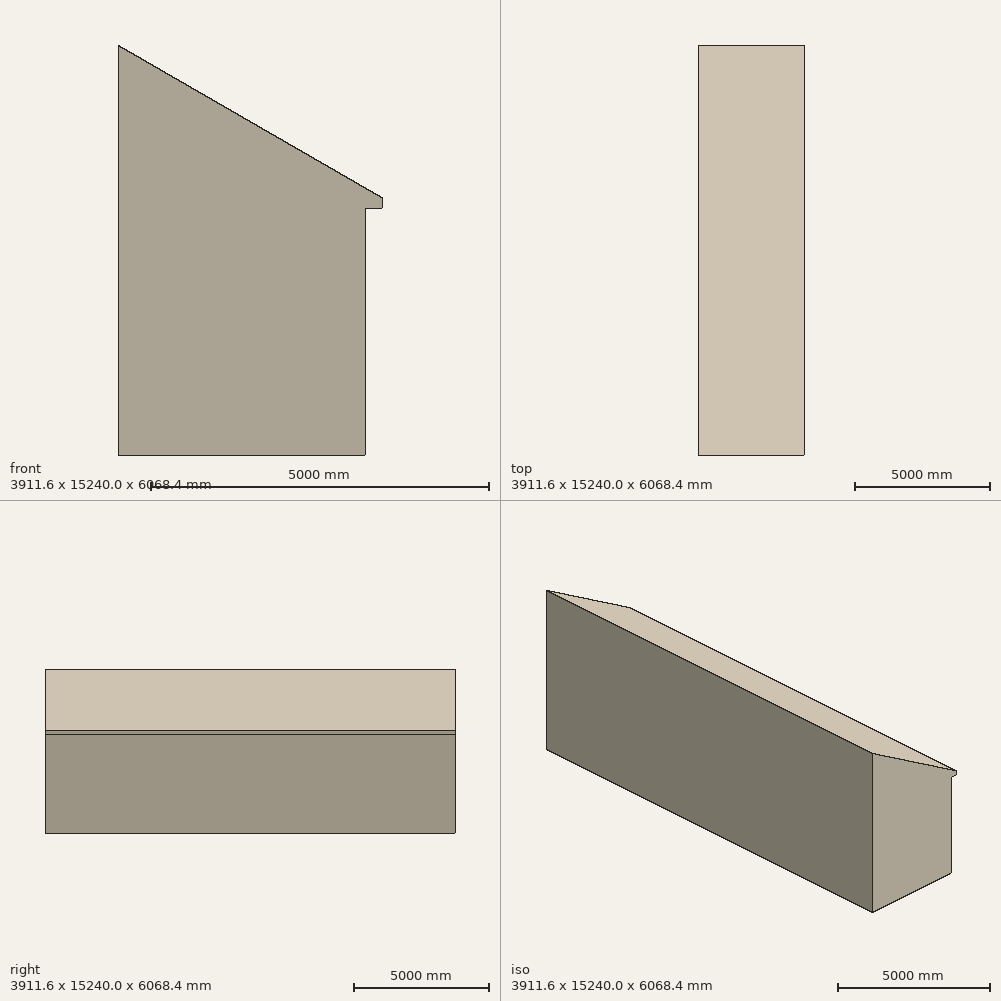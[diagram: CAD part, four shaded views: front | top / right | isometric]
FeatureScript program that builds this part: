
annotation { "Feature Type Name" : "Feature", "Feature Type Description" : "" }
export const myFeature = defineFeature(function(context is Context, id is Id, definition is map)
    precondition{}
    {
        {
            var Q0;
            Q0=qCreatedBy(makeId("Front.planeOp"),FACE);
            var sketch = newSketch(context, id + "F0", { "sketchPlane" : qUnion([Q0])});
            skLineSegment(sketch, "E0", {"start": v(0, 0) * mm, "end": v(0, -3657.6) * mm});
            skLineSegment(sketch, "E1", {"start": v(0, -3657.6) * mm, "end": v(-3657.6, -3657.6) * mm});
            skLineSegment(sketch, "E2", {"start": v(-3657.6, -3657.6) * mm, "end": v(-3657.6, 2410.76) * mm});
            skLineSegment(sketch, "E3", {"start": v(-3657.6, 2410.76) * mm, "end": v(254, 152.4) * mm});
            skLineSegment(sketch, "E4", {"start": v(254, 152.4) * mm, "end": v(254, 0) * mm});
            skLineSegment(sketch, "E5", {"start": v(254, 0) * mm, "end": v(0, 0) * mm});
            skSolve(sketch);
        }
        {
            var Q0;
            Q0=makeQuery(id+"F0.imprint","IMPRINT",FACE,{"disambiguationData":[TD([[makeQuery(id+"F0.imprint","IMPRINT",EDGE,{"derivedFrom":sQuery(id+"F0.wireOp",EDGE,"E0")}),-1.0]])]});
            extrude(context, id + "F1", {"entities" : qUnion([Q0]), "depth" : 15240 * mm, "offsetDistance" : 25.4 * mm});
        }
    });
